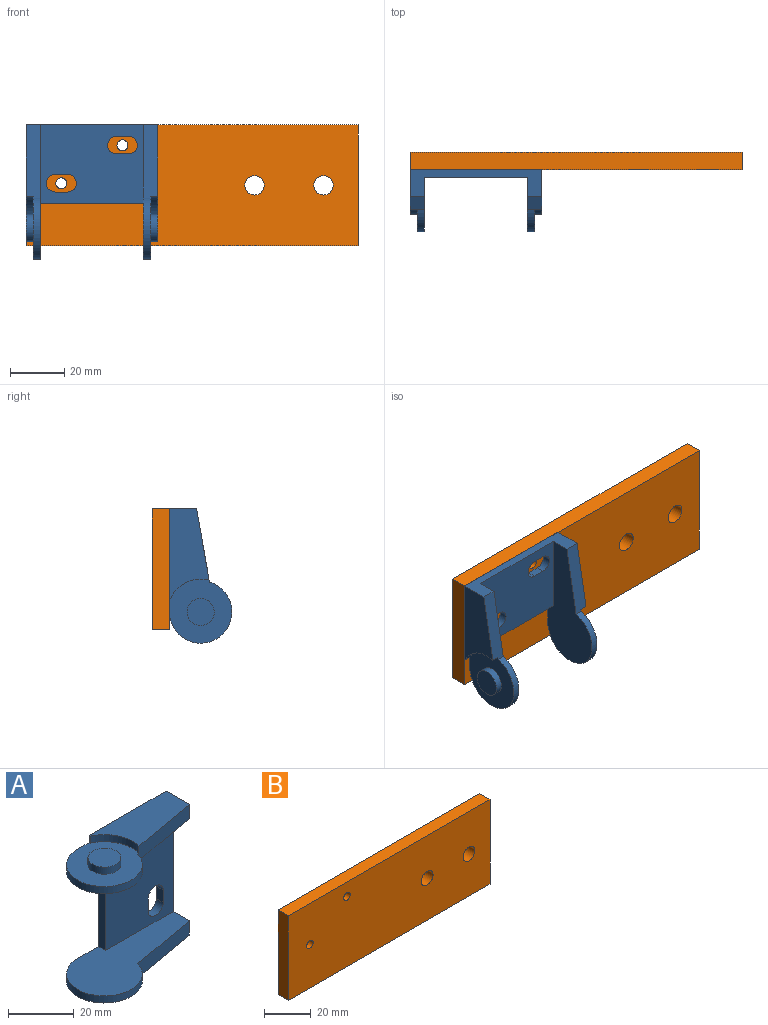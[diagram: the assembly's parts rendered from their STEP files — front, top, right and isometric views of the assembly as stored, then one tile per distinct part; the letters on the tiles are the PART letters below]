
ASSEMBLY  parts=2 mates=1
PART A: 30 faces, bbox 49.5x23x48.5 mm
  f0: cylinder r=11.5mm len=23mm, axis (0,0,-1), area 133.6mm2, adj f25,f27,f28,f29
  f1: cylinder r=12.1mm len=14.16mm, axis (0,0,1), area 44.7mm2, adj f23,f26,f27,f28
  f2: cylinder r=5mm len=10mm, axis (0,0,1), area 82.5mm2, adj f22,f27
  f3: cylinder r=11.5mm len=23mm, axis (0,0,-1), area 133.6mm2, adj f16,f20,f21,f25
  f4: cylinder r=12.1mm len=14.16mm, axis (0,0,1), area 44.7mm2, adj f18,f19,f20,f21
  f5: cylinder r=5mm len=10mm, axis (0,0,1), area 82.5mm2, adj f17,f20
  f6: plane 4.5x3mm, normal (-1,0,0), area 13.5mm2, adj f7,f9,f14,f25
  f7: cylinder r=3.25mm len=6.5mm, axis (0,-1,0), area 30.6mm2, adj f6,f8,f14,f25
  f8: plane 4.5x3mm, normal (1,0,0), area 13.5mm2, adj f7,f9,f14,f25
  f9: cylinder r=3.25mm len=6.5mm, axis (0,-1,0), area 30.6mm2, adj f6,f8,f14,f25
  f10: plane 4.5x3mm, normal (-1,0,0), area 13.5mm2, adj f11,f13,f14,f25
  f11: cylinder r=3.25mm len=6.5mm, axis (0,-1,0), area 30.6mm2, adj f10,f12,f14,f25
  f12: plane 4.5x3mm, normal (1,0,0), area 13.5mm2, adj f11,f13,f14,f25
  f13: cylinder r=3.25mm len=6.5mm, axis (0,-1,0), area 30.6mm2, adj f10,f12,f14,f25
  f14: plane 38x29mm, normal (0,-1,0), area 977.1mm2, adj f6,f7,f8,f9,f10,f11,f12,f13
  f15: plane 38x3mm, normal (-1,0,0), area 114mm2, adj f14,f16,f25,f29
  f16: plane 49.5x23mm, normal (0,0,-1), area 684.3mm2, adj f3,f14,f15,f21,f24,f25
  f17: plane 10x10mm, normal (0,0,1), area 78.5mm2, adj f5
  f18: plane 33x14.64mm, normal (0,0,1), area 343.9mm2, adj f4,f19,f21,f24,f25
  f19: plane 2.63x0.48mm, normal (-1,0,0), area 1.3mm2, adj f4,f18,f20,f25
  f20: plane 23.6x23mm, normal (0,0,1), area 348.8mm2, adj f3,f4,f5,f19,f21,f25
  f21: plane 26.97x5.25mm, normal (0.17,-0.98,0), area 142mm2, adj f3,f4,f16,f18,f20,f24
  f22: plane 10x10mm, normal (0,0,-1), area 78.5mm2, adj f2
  f23: plane 33x14.64mm, normal (0,0,-1), area 343.9mm2, adj f1,f24,f25,f26,f28
  f24: plane 48.5x10mm, normal (1,0,0), area 219mm2, adj f14,f16,f18,f21,f23,f25,f28,f29
  f25: plane 48.5x38mm, normal (0,1,0), area 1349.9mm2, adj f0,f3,f6,f7,f8,f9,f10,f11
  f26: plane 2.63x0.48mm, normal (-1,0,0), area 1.3mm2, adj f1,f23,f25,f27
  f27: plane 23.6x23mm, normal (0,0,-1), area 348.8mm2, adj f0,f1,f2,f25,f26,f28
  f28: plane 26.97x5.25mm, normal (0.17,-0.98,0), area 142mm2, adj f0,f1,f23,f24,f27,f29
  f29: plane 49.5x23mm, normal (0,0,1), area 684.3mm2, adj f0,f14,f15,f24,f25,f28
PART B: 10 faces, bbox 122.2x6.4x44.5 mm
  f0: plane 44.45x6.35mm, normal (-1,0,0), area 282.3mm2, adj f1,f3,f4,f5
  f1: plane 122.24x6.35mm, normal (0,0,-1), area 776.2mm2, adj f0,f2,f4,f5
  f2: plane 44.45x6.35mm, normal (1,0,0), area 282.3mm2, adj f1,f3,f4,f5
  f3: plane 122.24x6.35mm, normal (0,0,1), area 776.2mm2, adj f0,f2,f4,f5
  f4: plane 122.24x44.45mm, normal (0,1,0), area 5327.8mm2, adj f0,f1,f2,f3,f6,f7,f8,f9
  f5: plane 122.24x44.45mm, normal (0,-1,0), area 5327.8mm2, adj f0,f1,f2,f3,f6,f7,f8,f9
  f6: cylinder r=3.57mm len=7.14mm, axis (0,-1,0), area 142.4mm2, adj f4,f5
  f7: cylinder r=3.57mm len=7.14mm, axis (0,-1,0), area 142.4mm2, adj f4,f5
  f8: cylinder r=2.02mm len=6.35mm, axis (0,-1,0), area 80.6mm2, adj f4,f5
  f9: cylinder r=2.02mm len=6.35mm, axis (0,-1,0), area 80.6mm2, adj f4,f5
PLACE A rot(axis=(0,-1,0),90deg) t=(-17.05,-13.81,-15.12)mm
PLACE B t=(5,-2.31,0.6)mm
MATE fastened A.f25 <-> B.f9  axis (0,1,0) through (-24.8,-2.31,15.33)mm
